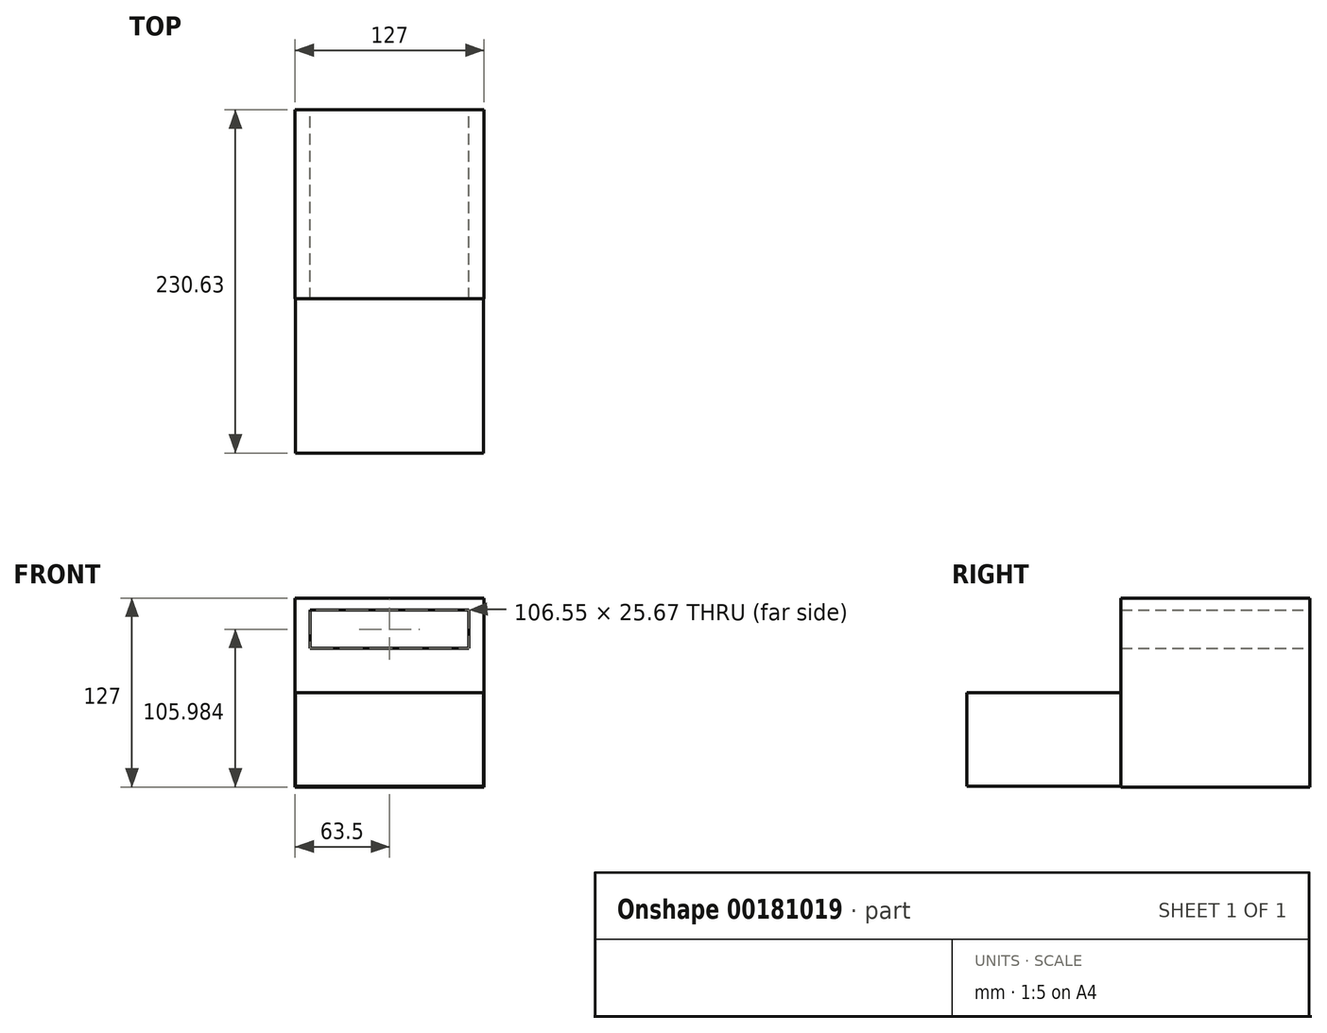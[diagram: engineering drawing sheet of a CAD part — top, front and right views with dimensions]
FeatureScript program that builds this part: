
annotation { "Feature Type Name" : "Feature", "Feature Type Description" : "" }
export const myFeature = defineFeature(function(context is Context, id is Id, definition is map)
    precondition{}
    {
        {
            var Q0;
            Q0=qCreatedBy(makeId("Front.planeOp"),FACE);
            var sketch = newSketch(context, id + "F0", { "sketchPlane" : qUnion([Q0])});
            skLineSegment(sketch, "E0.bottom", {"start": v(63.5, 63.5) * mm, "end": v(-63.5, 63.5) * mm});
            skLineSegment(sketch, "E0.top", {"start": v(63.5, -63.5) * mm, "end": v(-63.5, -63.5) * mm});
            skLineSegment(sketch, "E0.left", {"start": v(63.5, 63.5) * mm, "end": v(63.5, -63.5) * mm});
            skLineSegment(sketch, "E0.right", {"start": v(-63.5, 63.5) * mm, "end": v(-63.5, -63.5) * mm});
            skPoint(sketch, "E0.middle", {"position": v(0, 0) * mm});
            skLineSegment(sketch, "E1.bottom", {"start": v(-53.28, 55.32) * mm, "end": v(53.28, 55.32) * mm});
            skLineSegment(sketch, "E1.top", {"start": v(-53.28, 29.65) * mm, "end": v(53.28, 29.65) * mm});
            skLineSegment(sketch, "E1.left", {"start": v(-53.28, 55.32) * mm, "end": v(-53.28, 29.65) * mm});
            skLineSegment(sketch, "E1.right", {"start": v(53.28, 55.32) * mm, "end": v(53.28, 29.65) * mm});
            skPoint(sketch, "E1.middle", {"position": v(0, 42.48) * mm});
            skSolve(sketch);
        }
        {
            var Q0;
            Q0 = qSketchRegion(id + "F0", true);
            var Q1;
            Q1=makeQuery(id+"F0.imprint","IMPRINT",FACE,{"disambiguationData":[TD([[makeQuery(id+"F0.imprint","IMPRINT",EDGE,{"derivedFrom":sQuery(id+"F0.wireOp",EDGE,"E0.bottom")}),1.0]])]});
            extrude(context, id + "F1", {"entities" : qUnion([Q0, Q1]), "depth" : 127 * mm});
        }
        {
            var Q0;
            Q0=qCreatedBy(makeId("Front.planeOp"),FACE);
            var sketch = newSketch(context, id + "F2", { "sketchPlane" : qUnion([Q0])});
            skLineSegment(sketch, "E2.bottom", {"start": v(63, 0) * mm, "end": v(-63.26, 0) * mm});
            skLineSegment(sketch, "E2.top", {"start": v(63, -63.13) * mm, "end": v(-63.26, -63.13) * mm});
            skLineSegment(sketch, "E2.left", {"start": v(63, 0) * mm, "end": v(63, -63.13) * mm});
            skLineSegment(sketch, "E2.right", {"start": v(-63.26, 0) * mm, "end": v(-63.26, -63.13) * mm});
            skSolve(sketch);
        }
        {
            var Q0;
            Q0 = qSketchRegion(id + "F2", true);
            extrude(context, id + "F3", {"entities" : qUnion([Q0]), "operationType" : NewBodyOperationType.ADD, "depth" : 230.63 * mm});
        }
    });
